# Revit family: RUFO-320-1300-830-Zx
name_source: partatom
category: Oprawy oświetleniowe
revit_build: Autodesk Revit 2017 (Build: 20190507_1515(x64)
units: mm (PartAtom-declared; Revit-internal decimal feet)

## family parameters
Numer OmniClass = 23.80.70.11
Obiekt nadrzędny = Powierzchnia
Punkt obliczania pomieszczeń = Nie
Tnij formami wycięć po wczytaniu = Tak
Typ części = Normalny
Tytuł OmniClass = Luminaries for Internal Lighting
Współdzielony = Nie
Wymiar okrągłego złącza = Użyj średnicy
Źródło światła = Tak

## types (9) — shared parameters
Emituj kształt widoczny w renderingu = Nie
Emituj ze średnicy okręgu = 300 mm
Filtr koloru = 16777215
Kod zespołu = D5020200
Lampa = LED
Obciążenie pozorne = 10 VA
Odchylenie kierunku = 90.00°
Plik sieci fotometrycznej = RUFO 3201300-840-Z.IES
Producent = RIDI Leuchten GmbH
URL = www.ridi.de
Zmiana temperatury barwowej przyciemniania lampy = <Brak>
brand = RIDI
conformity mark = CE
electrical safety class = 1
height = 85 mm  [stored 0.278871 ft]
ingress protection (IP) code = IP20
length = 300 mm
nominal frequency = 50-60Hz
nominal voltage = 230
rated input power = 10
voltage type (AC, DC, UC) = AC
width = 300 mm
zero-valued in all types: Domyślna rzędna

## per-type parameters (varying)
| type | Model | product name | weight |
| RUFO 320/1300-830 Z | 0420758 | RUFO 320/1300-830 Z | 0.8kg |
| RUFO 320/1300-830 Z-DALI | 0430758 | RUFO 320/1300-830 Z-DALI | 0.8kg |
| RUFO 320/1300-830 Z-2K | 0420759 | RUFO 320/1300-830 Z-2K | 0.8kg |
| RUFO 320/1300-830 Z-2K-EDS3 | 0420759//377 | RUFO 320/1300-830 Z-2K-EDS3 | 0.8kg |
| RUFO 320/1300-830 Z-2K-RS | 0420759//396 | RUFO 320/1300-830 Z-2K-RS | 0.8kg |
| RUFO 320/1300-830 Z-2K-RS-EDS3 | 0420759//377396 | RUFO 320/1300-830 Z-2K-RS-EDS3 | 0.8kg |
| RUFO 320/1300-830 Z-EDS3 | 0420758//377 | RUFO 320/1300-830 Z-EDS3 | 0.92kg |
| RUFO 320/1300-830 Z-RS | 0420758//377 | RUFO 320/1300-830 Z-EDS3 | 0.8kg |
| RUFO 320/1300-830 Z-RS-EDS3 | 0420758//377396 | RUFO 320/1300-830 Z-RS-EDS3 | 0.8kg |

note: [stored X ft] marks values corroborated as IEEE doubles in the binary element streams (Revit-internal decimal feet)
